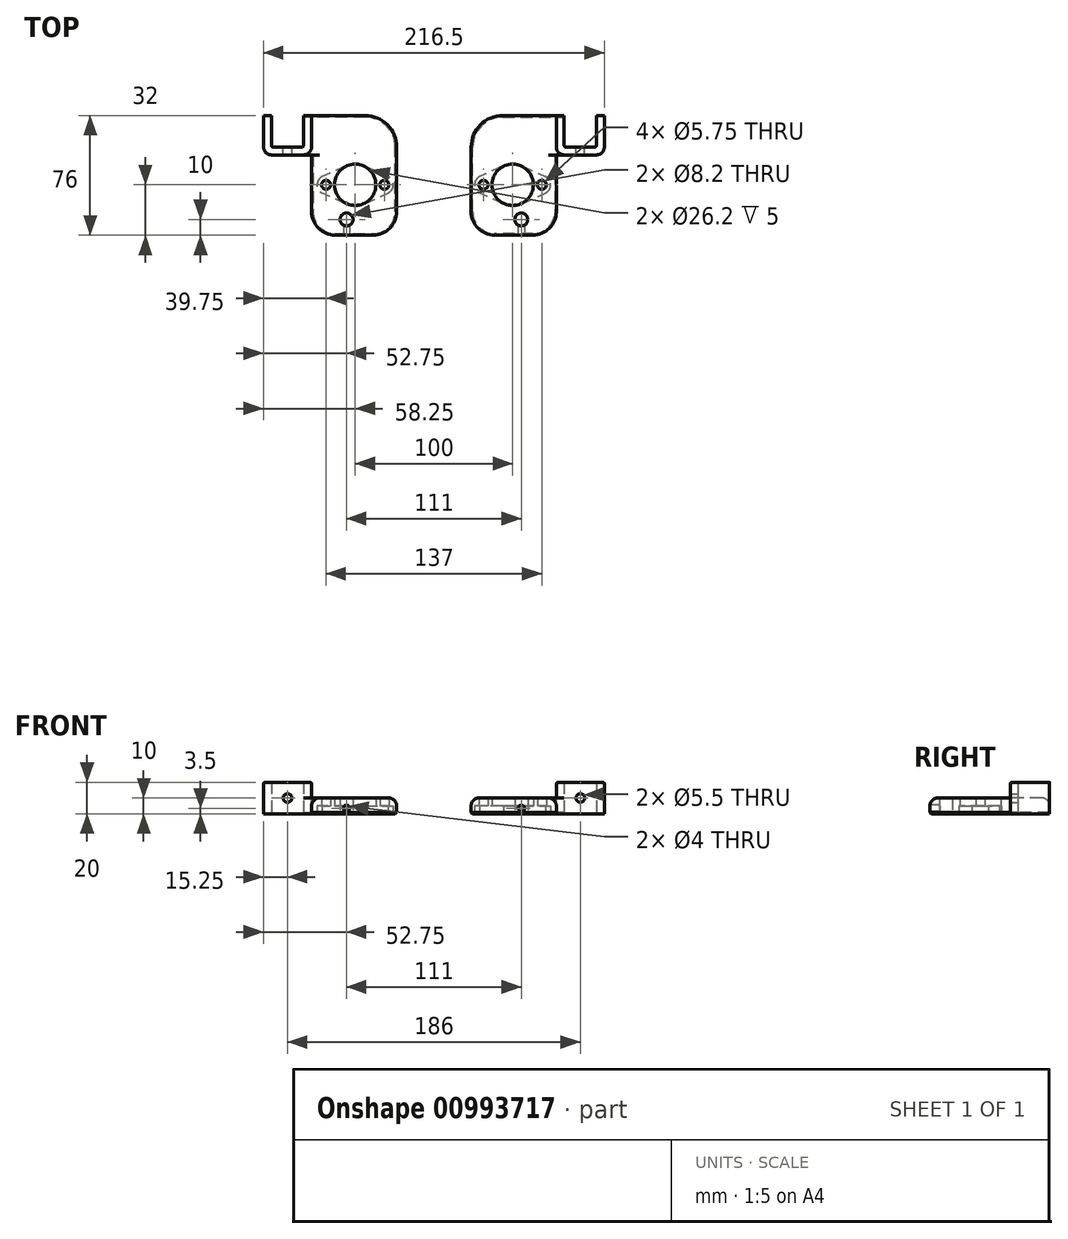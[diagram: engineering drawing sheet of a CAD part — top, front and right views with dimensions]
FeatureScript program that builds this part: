
annotation { "Feature Type Name" : "Feature", "Feature Type Description" : "" }
export const myFeature = defineFeature(function(context is Context, id is Id, definition is map)
    precondition{}
    {
        {
            var Q0;
            Q0=qCreatedBy(makeId("Top.planeOp"),FACE);
            var sketch = newSketch(context, id + "F0", { "sketchPlane" : qUnion([Q0])});
            skArc(sketch, "E0", {"start": v(10.42, -7.94) * mm, "mid": v(0, 13.1) * mm, "end": v(-10.42, -7.94) * mm});
            skCircle(sketch, "E1", {"center": v(-18.5, 0) * mm, "radius": 2.88 * mm});
            skCircle(sketch, "E2", {"center": v(18.5, 0) * mm, "radius": 2.88 * mm});
            skLineSegment(sketch, "E3.bottom", {"start": v(32.75, 44) * mm, "end": v(53.25, 44) * mm});
            skLineSegment(sketch, "E3.top", {"start": v(32.75, 24) * mm, "end": v(53.25, 24) * mm});
            skLineSegment(sketch, "E3.left", {"start": v(32.75, 44) * mm, "end": v(32.75, 24) * mm});
            skLineSegment(sketch, "E3.right", {"start": v(53.25, 44) * mm, "end": v(53.25, 24) * mm});
            skLineSegment(sketch, "E4.bottom", {"start": v(-6.38, 44) * mm, "end": v(58.25, 44) * mm});
            skLineSegment(sketch, "E4.right", {"start": v(58.25, 44) * mm, "end": v(58.25, 24) * mm});
            skLineSegment(sketch, "E5", {"start": v(43, 24) * mm, "end": v(43, 44) * mm, "construction": true});
            skLineSegment(sketch, "E6.top", {"start": v(53.25, 19) * mm, "end": v(43, 19) * mm});
            skPoint(sketch, "E7.visualSharp", {"position": v(-23, 44) * mm});
            skArc(sketch, "E7.filletArc", {"start": v(-6.38, 44) * mm, "mid": v(-20.52, 38.14) * mm, "end": v(-26.38, 24) * mm});
            skPoint(sketch, "E8.visualSharp", {"position": v(23, 19) * mm});
            skPoint(sketch, "E9.visualSharp", {"position": v(58.25, 19) * mm});
            skArc(sketch, "E9.filletArc", {"start": v(53.25, 19) * mm, "mid": v(56.79, 20.46) * mm, "end": v(58.25, 24) * mm});
            skLineSegment(sketch, "E10", {"start": v(27.75, 44) * mm, "end": v(27.75, 11.94) * mm});
            skCircle(sketch, "E11", {"center": v(5.5, -22) * mm, "radius": 4.1 * mm});
            skLineSegment(sketch, "E12", {"start": v(-26.38, 24) * mm, "end": v(-26.38, -17) * mm});
            skLineSegment(sketch, "E13", {"start": v(-11.37, -32) * mm, "end": v(12.75, -32) * mm});
            skLineSegment(sketch, "E14", {"start": v(27.75, -17) * mm, "end": v(27.75, 11.94) * mm});
            skLineSegment(sketch, "E15", {"start": v(43, 19) * mm, "end": v(27.75, 19) * mm});
            skCircle(sketch, "E16", {"center": v(0, 0) * mm, "radius": 13.1 * mm});
            skPoint(sketch, "E17.visualSharp", {"position": v(-26.37, -32) * mm});
            skArc(sketch, "E17.filletArc", {"start": v(-26.37, -17) * mm, "mid": v(-21.98, -27.6) * mm, "end": v(-11.37, -32) * mm});
            skPoint(sketch, "E18.visualSharp", {"position": v(27.75, -32) * mm});
            skArc(sketch, "E18.filletArc", {"start": v(12.75, -32) * mm, "mid": v(23.36, -27.6) * mm, "end": v(27.75, -17) * mm});
            skSolve(sketch);
        }
        {
            var Q0;
            Q0=makeQuery(id+"F0.imprint","IMPRINT",FACE,{"disambiguationData":[TD([[makeQuery(id+"F0.imprint","IMPRINT",EDGE,{"derivedFrom":sQuery(id+"F0.wireOp",EDGE,"E0")}),-1.0]])]});
            var Q1;
            Q1=makeQuery(id+"F0.imprint","IMPRINT",FACE,{"disambiguationData":[TD([[makeQuery(id+"F0.imprint","IMPRINT",EDGE,{"derivedFrom":sQuery(id+"F0.wireOp",EDGE,"E1")}),-1.0]])]});
            extrude(context, id + "F1", {"entities" : qUnion([Q0, Q1]), "depth" : 10 * mm, "offsetDistance" : 25 * mm});
        }
        {
            var Q0;
            Q0=makeQuery(id+"F0.imprint","IMPRINT",FACE,{"disambiguationData":[TD([[makeQuery(id+"F0.imprint","IMPRINT",EDGE,{"derivedFrom":sQuery(id+"F0.wireOp",EDGE,"E3.top")}),-1.0]])]});
            extrude(context, id + "F2", {"entities" : qUnion([Q0]), "operationType" : NewBodyOperationType.ADD, "depth" : 20 * mm, "offsetDistance" : 25 * mm});
        }
        {
            var Q0;
            Q0=makeQuery(id+"F2.opExtrude","SWEPT_FACE",FACE,{"disambiguationData":[OSD([sQuery(id+"F0.wireOp",EDGE,"E3.top")])]});
            var sketch = newSketch(context, id + "F3", { "sketchPlane" : qUnion([Q0])});
            skCircle(sketch, "E19", {"center": v(-43, 10) * mm, "radius": 2.75 * mm});
            skPoint(sketch, "E19.centerSnap0", {"position": v(-43, 20) * mm});
            skSolve(sketch);
        }
        {
            var Q0;
            Q0=makeQuery(id+"F3.imprint","IMPRINT",FACE,{"disambiguationData":[TD([[makeQuery(id+"F3.imprint","IMPRINT",EDGE,{"derivedFrom":sQuery(id+"F3.wireOp",EDGE,"E19")}),1.0]])]});
            extrude(context, id + "F4", {"entities" : qUnion([Q0]), "operationType" : NewBodyOperationType.REMOVE, "oppositeDirection" : true, "depth" : 25 * mm, "offsetDistance" : 25 * mm});
        }
        {
            var Q0;
            Q0=makeQuery(id+"F1.opExtrude","SWEPT_FACE",FACE,{"disambiguationData":[OSD([sQuery(id+"F0.wireOp",EDGE,"E13")])]});
            var sketch = newSketch(context, id + "F5", { "sketchPlane" : qUnion([Q0])});
            skLineSegment(sketch, "E20.0", {"start": v(1.4, 0) * mm, "end": v(9.6, 0) * mm});
            skCircle(sketch, "E21", {"center": v(5.5, 3.5) * mm, "radius": 2 * mm});
            skPoint(sketch, "E21.centerSnap0", {"position": v(5.5, 0) * mm});
            skSolve(sketch);
        }
        {
            var Q0;
            Q0=makeQuery(id+"F5.imprint","IMPRINT",FACE,{"disambiguationData":[TD([[makeQuery(id+"F5.imprint","IMPRINT",EDGE,{"derivedFrom":sQuery(id+"F5.wireOp",EDGE,"E21")}),1.0]])]});
            extrude(context, id + "F6", {"entities" : qUnion([Q0]), "operationType" : NewBodyOperationType.REMOVE, "oppositeDirection" : true, "depth" : 6.5 * mm, "offsetDistance" : 25 * mm});
        }
        {
            var Q0;
            {var subQ0=sQuery(id+"F0.wireOp",EDGE,"E14");var subQ1=sQuery(id+"F0.wireOp",EDGE,"E10");Q0=makeQuery(id+"F2.boolean.opBoolean","SPLIT",EDGE,{"disambiguationData":[topologyDisambiguationEdgeConnected([makeQuery(id+"F2.opExtrude","SWEPT_FACE",FACE,{"disambiguationData":[OSD([subQ1])]})])],"derivedFrom":makeQuery(id+"F1.opExtrude","CAP_EDGE",EDGE,{"disambiguationData":[OSD([subQ1,subQ0])],"isStart":false})});}
            fillet(context, id + "F7", {"entities" : qUnion([Q0]), "radius" : 5 * mm, "tangentPropagation" : true, "allowEdgeOverflow" : false});
        }
        {
            var Q0;
            {var subQ0=sQuery(id+"F0.wireOp",EDGE,"E14");var subQ1=sQuery(id+"F0.wireOp",EDGE,"E10");Q0=makeQuery(id+"F2.boolean.opBoolean","SPLIT",EDGE,{"disambiguationData":[topologyDisambiguationEdgeConnected([makeQuery(id+"F1.opExtrude","SWEPT_FACE",FACE,{"disambiguationData":[OSD([subQ1,subQ0])]})])],"derivedFrom":makeQuery(id+"F1.opExtrude","CAP_EDGE",EDGE,{"disambiguationData":[OSD([subQ1,subQ0])],"isStart":false})});}
            var Q1;
            Q1=makeQuery(id+"F2.opExtrude","CAP_EDGE",EDGE,{"disambiguationData":[OSD([sQuery(id+"F0.wireOp",EDGE,"E6.top"),sQuery(id+"F0.wireOp",EDGE,"E15")])],"isStart":false});
            var Q2;
            Q2=makeQuery(id+"F2.opExtrude","CAP_EDGE",EDGE,{"disambiguationData":[OSD([sQuery(id+"F0.wireOp",EDGE,"E10")])],"isStart":false});
            var Q3;
            Q3=makeQuery(id+"F2.opExtrude","SWEPT_EDGE",EDGE,{"disambiguationData":[OSD([sQuery(id+"F0.wireOp",EDGE,"E3.top"),sQuery(id+"F0.wireOp",EDGE,"E3.left")])]});
            var Q4;
            Q4=makeQuery(id+"F2.opExtrude","SWEPT_EDGE",EDGE,{"disambiguationData":[OSD([sQuery(id+"F0.wireOp",EDGE,"E3.top"),sQuery(id+"F0.wireOp",EDGE,"E3.right")])]});
            fillet(context, id + "F8", {"entities" : qUnion([Q0, Q1, Q2, Q3, Q4]), "radius" : 1 * mm, "tangentPropagation" : true, "allowEdgeOverflow" : false});
        }
        {
            var Q0;
            {var subQ0=sQuery(id+"F0.wireOp",EDGE,"E10");var subQ1=sQuery(id+"F0.wireOp",EDGE,"E15");Q0=makeQuery(id+"F2.boolean.opBoolean","SPLIT",EDGE,{"disambiguationData":[topologyDisambiguationEdgeConnected([makeQuery(id+"F1.opExtrude","SWEPT_FACE",FACE,{"disambiguationData":[OSD([subQ0,sQuery(id+"F0.wireOp",EDGE,"E14")])]})])],"derivedFrom":makeQuery(id+"F2.opExtrude","SWEPT_EDGE",EDGE,{"disambiguationData":[OSD([subQ0,subQ1])]})});}
            fillet(context, id + "F9", {"entities" : qUnion([Q0]), "radius" : 5 * mm, "tangentPropagation" : true, "allowEdgeOverflow" : false});
        }
        {
            var Q0;
            Q0=makeQuery(id+"F1.opExtrude","CAP_EDGE",EDGE,{"disambiguationData":[OSD([sQuery(id+"F0.wireOp",EDGE,"E7.filletArc")])],"isStart":true});
            chamfer(context, id + "F10", {"entities" : qUnion([Q0]), "width" : 1 * mm, "tangentPropagation" : true});
        }
        {
            var Q0;
            Q0=qCreatedBy(makeId("Right.planeOp"),FACE);
            cPlane(context, id + "F11", {"entities" : qUnion([Q0]), "cplaneType" : CPlaneType.OFFSET, "offset" : 50 * mm, "oppositeDirection" : true, "width" : 150 * mm, "height" : 150 * mm});
        }
        {
            var Q0;
            Q0=makeQuery(id+"F0.imprint","IMPRINT",FACE,{"disambiguationData":[TD([[makeQuery(id+"F0.imprint","IMPRINT",EDGE,{"derivedFrom":sQuery(id+"F0.wireOp",EDGE,"E1")}),-1.0]])]});
            var sketch = newSketch(context, id + "F12", { "sketchPlane" : qUnion([Q0])});
            skLineSegment(sketch, "E22", {"start": v(6.57, 11.84) * mm, "end": v(20.93, 5.26) * mm});
            skLineSegment(sketch, "E23", {"start": v(5.63, -12.27) * mm, "end": v(20.93, -5.26) * mm});
            skArc(sketch, "E24.trimOffspring", {"start": v(-6.55, -11.8) * mm, "mid": v(-0.52, -13.5) * mm, "end": v(5.63, -12.27) * mm});
            skPoint(sketch, "E25.center.orphan", {"position": v(-18.5, 0) * mm});
            skArc(sketch, "E26.trimOffspring", {"start": v(20.93, -5.26) * mm, "mid": v(24.17, 0) * mm, "end": v(20.93, 5.26) * mm});
            skArc(sketch, "E27.trimOffspring", {"start": v(13.5, -0.18) * mm, "mid": v(13.5, 0) * mm, "end": v(13.5, 0.18) * mm});
            skArc(sketch, "E28.trimOffspring", {"start": v(5.63, 12.27) * mm, "mid": v(-0.14, 13.5) * mm, "end": v(-5.89, 12.15) * mm});
            skLineSegment(sketch, "E29.MirrorCS", {"start": v(-6.57, 11.84) * mm, "end": v(-20.93, 5.26) * mm});
            skLineSegment(sketch, "E30.MirrorCS", {"start": v(-5.63, -12.27) * mm, "end": v(-20.93, -5.26) * mm});
            skArc(sketch, "E31.MirrorCS", {"start": v(-20.93, -5.26) * mm, "mid": v(-24.17, 0) * mm, "end": v(-20.93, 5.26) * mm});
            skLineSegment(sketch, "E32", {"start": v(-6.57, 11.84) * mm, "end": v(-5.89, 12.15) * mm});
            skLineSegment(sketch, "E33", {"start": v(5.63, 12.27) * mm, "end": v(6.57, 11.84) * mm});
            skSolve(sketch);
        }
        {
            var Q0;
            Q0=makeQuery(id+"F12.imprint","IMPRINT",FACE,{"disambiguationData":[TD([[makeQuery(id+"F12.imprint","IMPRINT",EDGE,{"derivedFrom":sQuery(id+"F12.wireOp",EDGE,"E23")}),1.0]])]});
            extrude(context, id + "F13", {"entities" : qUnion([Q0]), "operationType" : NewBodyOperationType.REMOVE, "depth" : 5 * mm, "offsetDistance" : 25 * mm});
        }
        {
            var Q0;
            Q0=makeQuery(id+"F1.opExtrude","SWEPT_BODY",BODY,{"disambiguationData":[OSD([sQuery(id+"F0.wireOp",EDGE,"E1"),sQuery(id+"F0.wireOp",EDGE,"E2"),sQuery(id+"F0.wireOp",EDGE,"E4.bottom"),sQuery(id+"F0.wireOp",EDGE,"E7.filletArc"),sQuery(id+"F0.wireOp",EDGE,"E10"),sQuery(id+"F0.wireOp",EDGE,"E11"),sQuery(id+"F0.wireOp",EDGE,"E12"),sQuery(id+"F0.wireOp",EDGE,"E13"),sQuery(id+"F0.wireOp",EDGE,"E14"),sQuery(id+"F0.wireOp",EDGE,"E16"),sQuery(id+"F0.wireOp",EDGE,"E17.filletArc"),sQuery(id+"F0.wireOp",EDGE,"E18.filletArc")])]});
            var Q1;
            Q1=qCreatedBy(id+"F11.planeOp",FACE);
            mirror(context, id + "F14", {"entities" : qUnion([Q0]), "mirrorPlane" : qUnion([Q1])});
        }
    });
